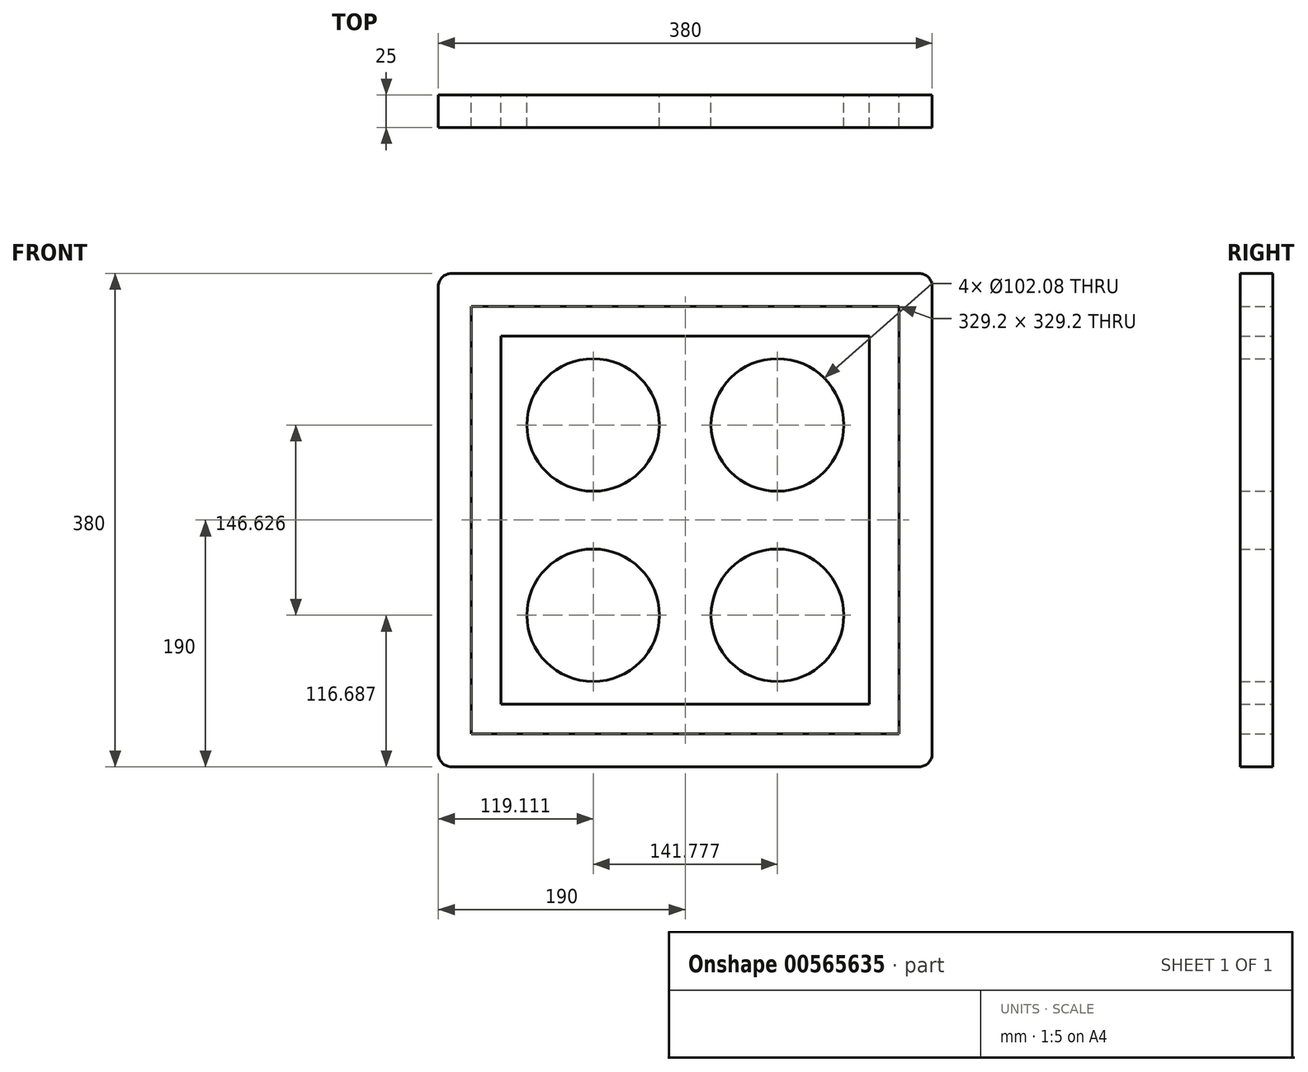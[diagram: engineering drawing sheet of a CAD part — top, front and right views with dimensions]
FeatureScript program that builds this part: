
annotation { "Feature Type Name" : "Feature", "Feature Type Description" : "" }
export const myFeature = defineFeature(function(context is Context, id is Id, definition is map)
    precondition{}
    {
        {
            var Q0;
            Q0=qCreatedBy(makeId("Front.planeOp"),FACE);
            var sketch = newSketch(context, id + "F0", { "sketchPlane" : qUnion([Q0])});
            skLineSegment(sketch, "E0.bottom", {"start": v(-180, 190) * mm, "end": v(180, 190) * mm});
            skLineSegment(sketch, "E0.top", {"start": v(-180, -190) * mm, "end": v(180, -190) * mm});
            skLineSegment(sketch, "E0.left", {"start": v(-190, 180) * mm, "end": v(-190, -180) * mm});
            skLineSegment(sketch, "E0.right", {"start": v(190, 180) * mm, "end": v(190, -180) * mm});
            skPoint(sketch, "E0.middle", {"position": v(0, 0) * mm});
            skLineSegment(sketch, "E1.bottom", {"start": v(-177.3, 177.3) * mm, "end": v(177.3, 177.3) * mm});
            skLineSegment(sketch, "E1.top", {"start": v(-177.3, -177.3) * mm, "end": v(177.3, -177.3) * mm});
            skLineSegment(sketch, "E1.left", {"start": v(-177.3, 177.3) * mm, "end": v(-177.3, -177.3) * mm});
            skLineSegment(sketch, "E1.right", {"start": v(177.3, 177.3) * mm, "end": v(177.3, -177.3) * mm});
            skLineSegment(sketch, "E2.bottom", {"start": v(-141.78, 141.78) * mm, "end": v(141.78, 141.78) * mm});
            skLineSegment(sketch, "E2.top", {"start": v(-141.78, -141.78) * mm, "end": v(141.78, -141.78) * mm});
            skLineSegment(sketch, "E2.left", {"start": v(-141.78, 141.78) * mm, "end": v(-141.78, -141.78) * mm});
            skLineSegment(sketch, "E2.right", {"start": v(141.78, 141.78) * mm, "end": v(141.78, -141.78) * mm});
            skCircle(sketch, "E3", {"center": v(-70.89, 73.31) * mm, "radius": 51.04 * mm});
            skPoint(sketch, "E3.centerSnap0", {"position": v(-70.89, 0) * mm});
            skPoint(sketch, "E3.centerSnap1", {"position": v(0, 73.31) * mm});
            skCircle(sketch, "E4", {"center": v(70.89, 73.31) * mm, "radius": 51.04 * mm});
            skPoint(sketch, "E4.centerSnap0", {"position": v(70.89, 0) * mm});
            skCircle(sketch, "E5", {"center": v(-70.89, -73.31) * mm, "radius": 51.04 * mm});
            skPoint(sketch, "E5.centerSnap0", {"position": v(0, -73.31) * mm});
            skCircle(sketch, "E6", {"center": v(70.89, -73.31) * mm, "radius": 51.04 * mm});
            skCircle(sketch, "E7", {"center": v(-152.38, 152.38) * mm, "radius": 3.18 * mm});
            skCircle(sketch, "E8", {"center": v(-108.85, 152.38) * mm, "radius": 3.18 * mm});
            skCircle(sketch, "E9", {"center": v(-65.3, 152.38) * mm, "radius": 3.18 * mm});
            skCircle(sketch, "E10", {"center": v(-21.77, 152.38) * mm, "radius": 3.18 * mm});
            skCircle(sketch, "E11", {"center": v(21.77, 152.38) * mm, "radius": 3.18 * mm});
            skCircle(sketch, "E12", {"center": v(65.3, 152.38) * mm, "radius": 3.18 * mm});
            skCircle(sketch, "E13", {"center": v(108.85, 152.38) * mm, "radius": 3.18 * mm});
            skCircle(sketch, "E14", {"center": v(152.38, 152.38) * mm, "radius": 3.18 * mm});
            skCircle(sketch, "E15", {"center": v(152.38, 108.85) * mm, "radius": 3.18 * mm});
            skCircle(sketch, "E16", {"center": v(152.38, 65.3) * mm, "radius": 3.18 * mm});
            skCircle(sketch, "E17", {"center": v(152.38, 21.77) * mm, "radius": 3.18 * mm});
            skCircle(sketch, "E18", {"center": v(152.38, -21.77) * mm, "radius": 3.18 * mm});
            skCircle(sketch, "E19", {"center": v(152.38, -65.3) * mm, "radius": 3.18 * mm});
            skCircle(sketch, "E20", {"center": v(21.77, -152.38) * mm, "radius": 3.18 * mm});
            skCircle(sketch, "E21", {"center": v(65.3, -152.38) * mm, "radius": 3.18 * mm});
            skCircle(sketch, "E22", {"center": v(-21.77, -152.38) * mm, "radius": 3.18 * mm});
            skCircle(sketch, "E23", {"center": v(-108.85, -152.38) * mm, "radius": 3.18 * mm});
            skCircle(sketch, "E24", {"center": v(-65.3, -152.38) * mm, "radius": 3.18 * mm});
            skCircle(sketch, "E25", {"center": v(-152.38, -108.85) * mm, "radius": 3.18 * mm});
            skCircle(sketch, "E26", {"center": v(-152.38, -65.3) * mm, "radius": 3.18 * mm});
            skCircle(sketch, "E27", {"center": v(-152.38, -21.77) * mm, "radius": 3.18 * mm});
            skCircle(sketch, "E28", {"center": v(-152.38, 21.77) * mm, "radius": 3.18 * mm});
            skCircle(sketch, "E29", {"center": v(-152.38, 65.3) * mm, "radius": 3.18 * mm});
            skCircle(sketch, "E30", {"center": v(-152.38, 108.85) * mm, "radius": 3.18 * mm});
            skLineSegment(sketch, "E31", {"start": v(-152.38, 152.38) * mm, "end": v(-108.85, 152.38) * mm, "construction": true});
            skLineSegment(sketch, "E32", {"start": v(-108.85, 152.38) * mm, "end": v(-65.3, 152.38) * mm, "construction": true});
            skLineSegment(sketch, "E33", {"start": v(-65.3, 152.38) * mm, "end": v(-21.77, 152.38) * mm, "construction": true});
            skLineSegment(sketch, "E34", {"start": v(-21.77, 152.38) * mm, "end": v(21.77, 152.38) * mm, "construction": true});
            skLineSegment(sketch, "E35", {"start": v(21.77, 152.38) * mm, "end": v(65.3, 152.38) * mm, "construction": true});
            skLineSegment(sketch, "E36", {"start": v(65.3, 152.38) * mm, "end": v(108.85, 152.38) * mm, "construction": true});
            skLineSegment(sketch, "E37", {"start": v(108.85, 152.38) * mm, "end": v(152.38, 152.38) * mm, "construction": true});
            skLineSegment(sketch, "E38", {"start": v(152.38, 152.38) * mm, "end": v(152.38, 108.85) * mm, "construction": true});
            skLineSegment(sketch, "E39", {"start": v(152.38, 108.85) * mm, "end": v(152.38, 65.3) * mm, "construction": true});
            skLineSegment(sketch, "E40", {"start": v(152.38, 65.3) * mm, "end": v(152.38, 21.77) * mm, "construction": true});
            skLineSegment(sketch, "E41", {"start": v(152.38, 21.77) * mm, "end": v(152.38, -21.77) * mm, "construction": true});
            skLineSegment(sketch, "E42", {"start": v(152.38, -21.77) * mm, "end": v(152.38, -65.3) * mm, "construction": true});
            skLineSegment(sketch, "E43", {"start": v(152.38, -65.3) * mm, "end": v(152.38, -108.85) * mm, "construction": true});
            skLineSegment(sketch, "E44", {"start": v(65.3, -152.38) * mm, "end": v(21.77, -152.38) * mm, "construction": true});
            skLineSegment(sketch, "E45", {"start": v(21.77, -152.38) * mm, "end": v(-21.77, -152.38) * mm, "construction": true});
            skLineSegment(sketch, "E46", {"start": v(-21.77, -152.38) * mm, "end": v(-65.3, -152.38) * mm, "construction": true});
            skLineSegment(sketch, "E47", {"start": v(-65.3, -152.38) * mm, "end": v(-108.85, -152.38) * mm, "construction": true});
            skLineSegment(sketch, "E48", {"start": v(-108.85, -152.38) * mm, "end": v(-152.38, -152.38) * mm, "construction": true});
            skLineSegment(sketch, "E49", {"start": v(-152.38, -152.38) * mm, "end": v(-152.38, -108.85) * mm, "construction": true});
            skLineSegment(sketch, "E50", {"start": v(-152.38, -108.85) * mm, "end": v(-152.38, -65.3) * mm, "construction": true});
            skLineSegment(sketch, "E51", {"start": v(-152.38, -65.3) * mm, "end": v(-152.38, -21.77) * mm, "construction": true});
            skLineSegment(sketch, "E52", {"start": v(-152.38, -21.77) * mm, "end": v(-152.38, 21.77) * mm, "construction": true});
            skLineSegment(sketch, "E53", {"start": v(-152.38, 21.77) * mm, "end": v(-152.38, 65.3) * mm, "construction": true});
            skLineSegment(sketch, "E54", {"start": v(-152.38, 65.3) * mm, "end": v(-152.38, 108.85) * mm, "construction": true});
            skLineSegment(sketch, "E55", {"start": v(-152.38, 108.85) * mm, "end": v(-152.38, 152.38) * mm, "construction": true});
            skCircle(sketch, "E56", {"center": v(-152.38, -152.38) * mm, "radius": 3.18 * mm});
            skCircle(sketch, "E57", {"center": v(152.38, -108.85) * mm, "radius": 3.18 * mm});
            skCircle(sketch, "E58", {"center": v(152.38, -152.38) * mm, "radius": 3.18 * mm});
            skCircle(sketch, "E59", {"center": v(108.85, -152.38) * mm, "radius": 3.18 * mm});
            skLineSegment(sketch, "E60", {"start": v(152.38, -108.85) * mm, "end": v(152.38, -152.38) * mm, "construction": true});
            skLineSegment(sketch, "E61", {"start": v(152.38, -152.38) * mm, "end": v(108.85, -152.38) * mm, "construction": true});
            skLineSegment(sketch, "E62", {"start": v(108.85, -152.38) * mm, "end": v(65.3, -152.38) * mm, "construction": true});
            skLineSegment(sketch, "E63.bottom", {"start": v(-70.89, 73.31) * mm, "end": v(70.89, 73.31) * mm, "construction": true});
            skLineSegment(sketch, "E63.top", {"start": v(-70.89, -73.31) * mm, "end": v(70.89, -73.31) * mm, "construction": true});
            skLineSegment(sketch, "E63.left", {"start": v(-70.89, 73.31) * mm, "end": v(-70.89, -73.31) * mm, "construction": true});
            skLineSegment(sketch, "E63.right", {"start": v(70.89, 73.31) * mm, "end": v(70.89, -73.31) * mm, "construction": true});
            skLineSegment(sketch, "E64", {"start": v(-141.78, 141.78) * mm, "end": v(-70.89, 73.31) * mm, "construction": true});
            skLineSegment(sketch, "E65", {"start": v(-70.89, -73.31) * mm, "end": v(-141.78, -141.78) * mm, "construction": true});
            skLineSegment(sketch, "E66", {"start": v(70.89, 73.31) * mm, "end": v(141.78, 141.78) * mm, "construction": true});
            skLineSegment(sketch, "E67", {"start": v(70.89, -73.31) * mm, "end": v(141.78, -141.78) * mm, "construction": true});
            skLineSegment(sketch, "E68", {"start": v(-137.87, -168.56) * mm, "end": v(-26.3, -168.56) * mm, "construction": true});
            skLineSegment(sketch, "E69", {"start": v(-140.74, -155.86) * mm, "end": v(2.52, -155.86) * mm, "construction": true});
            skLineSegment(sketch, "E70", {"start": v(-134.8, -155.86) * mm, "end": v(-134.8, -177.3) * mm, "construction": true});
            skLineSegment(sketch, "E71", {"start": v(-134.8, -166.58) * mm, "end": v(-134.8, -190) * mm, "construction": true});
            skLineSegment(sketch, "E72", {"start": v(-141.78, 141.78) * mm, "end": v(-152.38, 152.38) * mm, "construction": true});
            skLineSegment(sketch, "E73", {"start": v(141.78, -141.78) * mm, "end": v(152.38, -152.38) * mm, "construction": true});
            skLineSegment(sketch, "E74", {"start": v(141.78, 141.78) * mm, "end": v(152.38, 152.38) * mm, "construction": true});
            skLineSegment(sketch, "E75", {"start": v(-141.78, -141.78) * mm, "end": v(-152.38, -152.38) * mm, "construction": true});
            skPoint(sketch, "E76.visualSharp", {"position": v(-190, 190) * mm});
            skArc(sketch, "E76.filletArc", {"start": v(-180, 190) * mm, "mid": v(-187.07, 187.07) * mm, "end": v(-190, 180) * mm});
            skPoint(sketch, "E77.visualSharp", {"position": v(190, 190) * mm});
            skArc(sketch, "E77.filletArc", {"start": v(190, 180) * mm, "mid": v(187.07, 187.07) * mm, "end": v(180, 190) * mm});
            skPoint(sketch, "E78.visualSharp", {"position": v(-190, -190) * mm});
            skArc(sketch, "E78.filletArc", {"start": v(-190, -180) * mm, "mid": v(-187.07, -187.07) * mm, "end": v(-180, -190) * mm});
            skPoint(sketch, "E79.visualSharp", {"position": v(190, -190) * mm});
            skArc(sketch, "E79.filletArc", {"start": v(180, -190) * mm, "mid": v(187.07, -187.07) * mm, "end": v(190, -180) * mm});
            skLineSegment(sketch, "E80.bottom", {"start": v(-164.6, 164.6) * mm, "end": v(164.6, 164.6) * mm});
            skLineSegment(sketch, "E80.top", {"start": v(-164.6, -164.6) * mm, "end": v(164.6, -164.6) * mm});
            skLineSegment(sketch, "E80.left", {"start": v(-164.6, 164.6) * mm, "end": v(-164.6, -164.6) * mm});
            skLineSegment(sketch, "E80.right", {"start": v(164.6, 164.6) * mm, "end": v(164.6, -164.6) * mm});
            skLineSegment(sketch, "E81", {"start": v(-177.3, 177.3) * mm, "end": v(177.3, -177.3) * mm, "construction": true});
            skLineSegment(sketch, "E82", {"start": v(-177.3, -177.3) * mm, "end": v(177.3, 177.3) * mm, "construction": true});
            skLineSegment(sketch, "E83", {"start": v(-164.6, 164.6) * mm, "end": v(-164.6, 177.3) * mm, "construction": true});
            skLineSegment(sketch, "E84", {"start": v(164.6, 164.6) * mm, "end": v(164.6, 177.3) * mm, "construction": true});
            skSolve(sketch);
        }
        {
            var Q0;
            Q0=makeQuery(id+"F0.imprint","IMPRINT",FACE,{"disambiguationData":[TD([[makeQuery(id+"F0.imprint","IMPRINT",EDGE,{"derivedFrom":sQuery(id+"F0.wireOp",EDGE,"E0.bottom")}),-1.0]])]});
            var Q1;
            Q1=makeQuery(id+"F0.imprint","IMPRINT",FACE,{"disambiguationData":[TD([[makeQuery(id+"F0.imprint","IMPRINT",EDGE,{"derivedFrom":sQuery(id+"F0.wireOp",EDGE,"E1.bottom")}),-1.0]])]});
            var Q2;
            Q2=makeQuery(id+"F0.imprint","IMPRINT",FACE,{"disambiguationData":[TD([[makeQuery(id+"F0.imprint","IMPRINT",EDGE,{"derivedFrom":sQuery(id+"F0.wireOp",EDGE,"E2.bottom")}),-1.0]])]});
            extrude(context, id + "F1", {"entities" : qUnion([Q0, Q1, Q2]), "depth" : 25 * mm, "offsetDistance" : 25 * mm});
        }
    });
